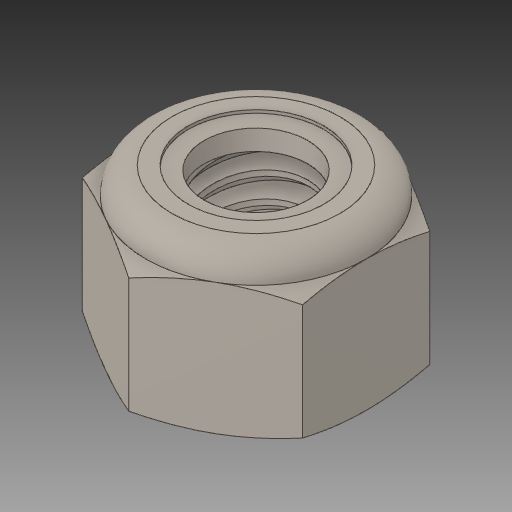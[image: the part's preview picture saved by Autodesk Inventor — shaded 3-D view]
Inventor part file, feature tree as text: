
AUTODESK INVENTOR PART (.ipt)
format: ipt  version: 2017.1 (Build 211199000, 199)  size: 307,712 bytes
history: native  units: in
note: dims shown in document units (in); Inventor stores cm internally (conversion verified against a paired STEP export)
features: other x1, revolve x1
ambient origin geometry x8: Origin, YZ Plane, XZ Plane, XY Plane, X Axis, Y Axis, Z Axis, Center Point
bodies: Solid1 (feature_tree), Solid2 (feature_tree)
feature tree (2):
  other  "Cut-Revolve4"
  revolve  "Revolve2"  [1 undecoded]
note: 1 required parameter value undecoded (feature->parameter linkage not recoverable at this tier; creation-order binding heuristic only, values carry confidence <= 0.55)
